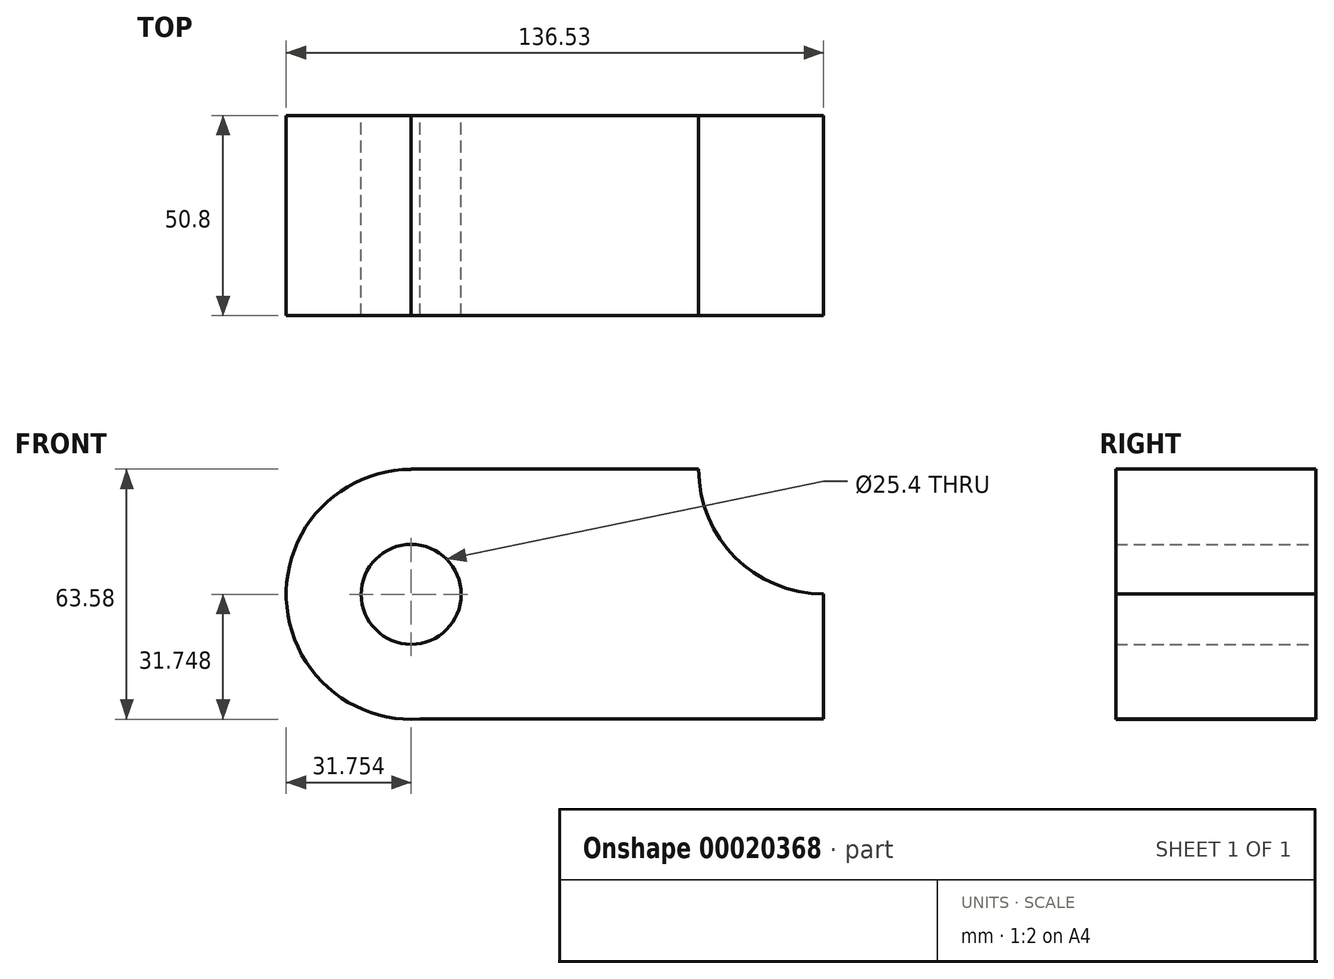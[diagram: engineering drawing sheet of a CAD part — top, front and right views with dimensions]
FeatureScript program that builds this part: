
annotation { "Feature Type Name" : "Feature", "Feature Type Description" : "" }
export const myFeature = defineFeature(function(context is Context, id is Id, definition is map)
    precondition{}
    {
        {
            var Q0;
            Q0=qCreatedBy(makeId("Front.planeOp"),FACE);
            var sketch = newSketch(context, id + "F0", { "sketchPlane" : qUnion([Q0])});
            skLineSegment(sketch, "E0.bottom", {"start": v(-47.7, 31.46) * mm, "end": v(25.33, 31.46) * mm});
            skLineSegment(sketch, "E0.top", {"start": v(-47.7, -32.04) * mm, "end": v(57.08, -32.04) * mm});
            skLineSegment(sketch, "E0.left", {"start": v(-47.7, 31.46) * mm, "end": v(-47.7, 31.38) * mm});
            skLineSegment(sketch, "E0.right", {"start": v(57.08, -0.29) * mm, "end": v(57.08, -32.04) * mm});
            skArc(sketch, "E1", {"start": v(-47.7, 31.38) * mm, "mid": v(-79.43, -1.53) * mm, "end": v(-45.38, -32.04) * mm});
            skArc(sketch, "E2", {"start": v(25.33, 31.46) * mm, "mid": v(34.63, 9.01) * mm, "end": v(57.08, -0.29) * mm});
            skCircle(sketch, "E3", {"center": v(-47.7, -0.37) * mm, "radius": 12.7 * mm});
            skSolve(sketch);
        }
        {
            var Q0;
            Q0=makeQuery(id+"F0.imprint","IMPRINT",FACE,{"disambiguationData":[TD([[makeQuery(id+"F0.imprint","IMPRINT",EDGE,{"derivedFrom":sQuery(id+"F0.wireOp",EDGE,"E0.bottom")}),-1.0]])]});
            extrude(context, id + "F1", {"entities" : qUnion([Q0]), "depth" : 50.8 * mm});
        }
    });
